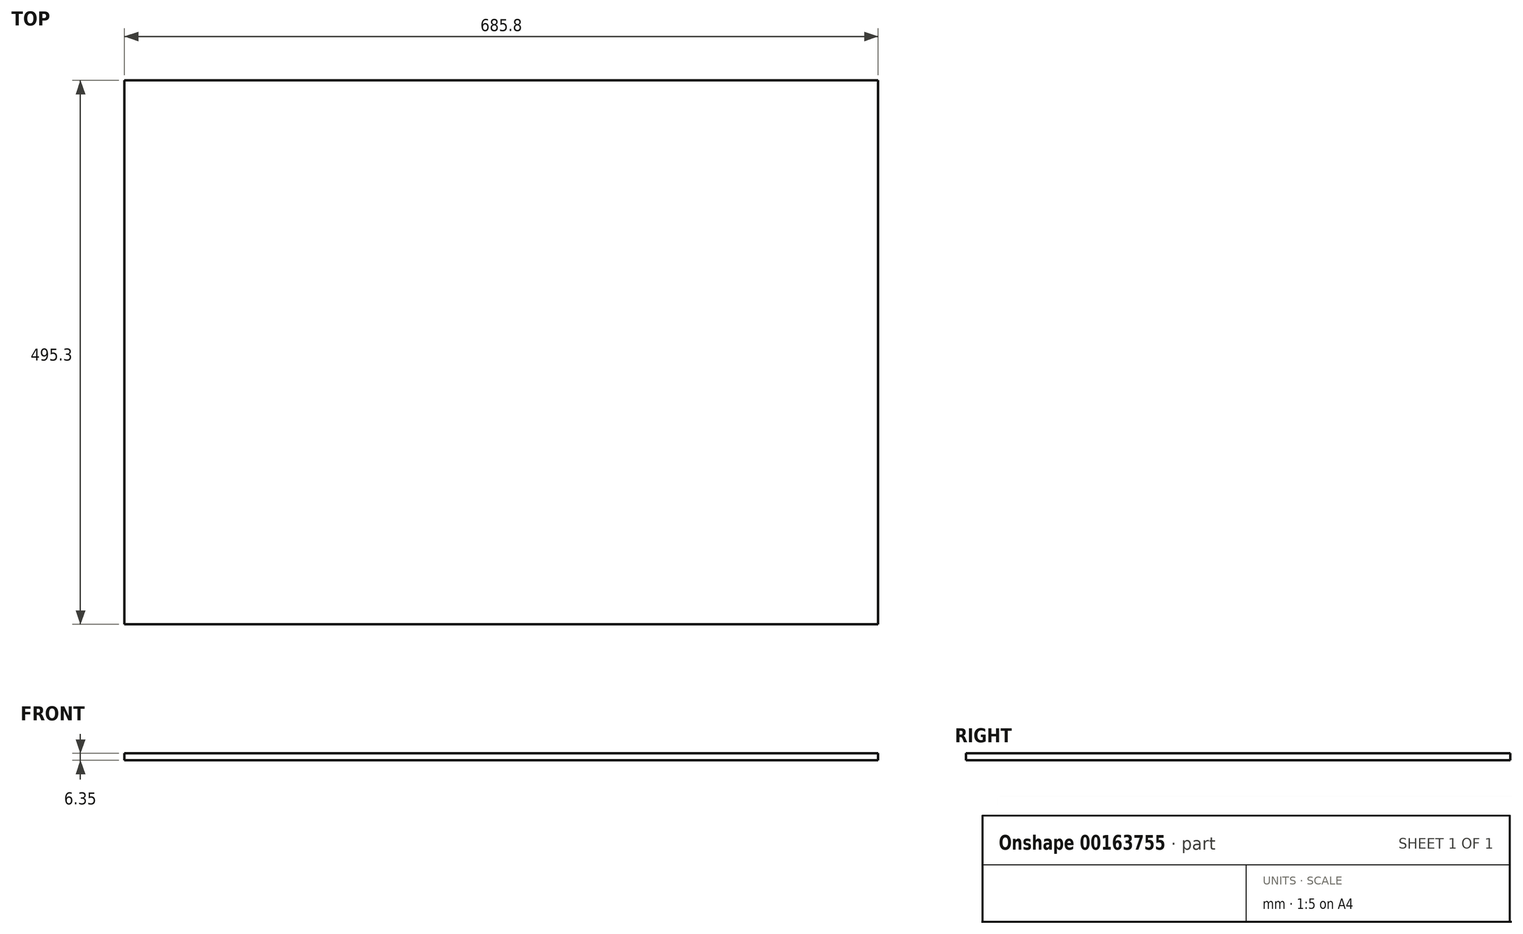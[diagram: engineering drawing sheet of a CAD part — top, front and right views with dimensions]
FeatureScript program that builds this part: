
annotation { "Feature Type Name" : "Feature", "Feature Type Description" : "" }
export const myFeature = defineFeature(function(context is Context, id is Id, definition is map)
    precondition{}
    {
        {
            var Q0;
            Q0=qCreatedBy(makeId("Top.planeOp"),FACE);
            var sketch = newSketch(context, id + "F0", { "sketchPlane" : qUnion([Q0])});
            skLineSegment(sketch, "E0.bottom", {"start": v(342.9, 247.65) * mm, "end": v(-342.9, 247.65) * mm});
            skLineSegment(sketch, "E0.top", {"start": v(342.9, -247.65) * mm, "end": v(-342.9, -247.65) * mm});
            skLineSegment(sketch, "E0.left", {"start": v(342.9, 247.65) * mm, "end": v(342.9, -247.65) * mm});
            skLineSegment(sketch, "E0.right", {"start": v(-342.9, 247.65) * mm, "end": v(-342.9, -247.65) * mm});
            skPoint(sketch, "E0.middle", {"position": v(0, 0) * mm});
            skSolve(sketch);
        }
        {
            var Q0;
            Q0=qSketchRegion(id+"F0",true);
            extrude(context, id + "F1", {"entities" : qUnion([Q0]), "depth" : 6.35 * mm, "offsetDistance" : 25.4 * mm});
        }
    });
